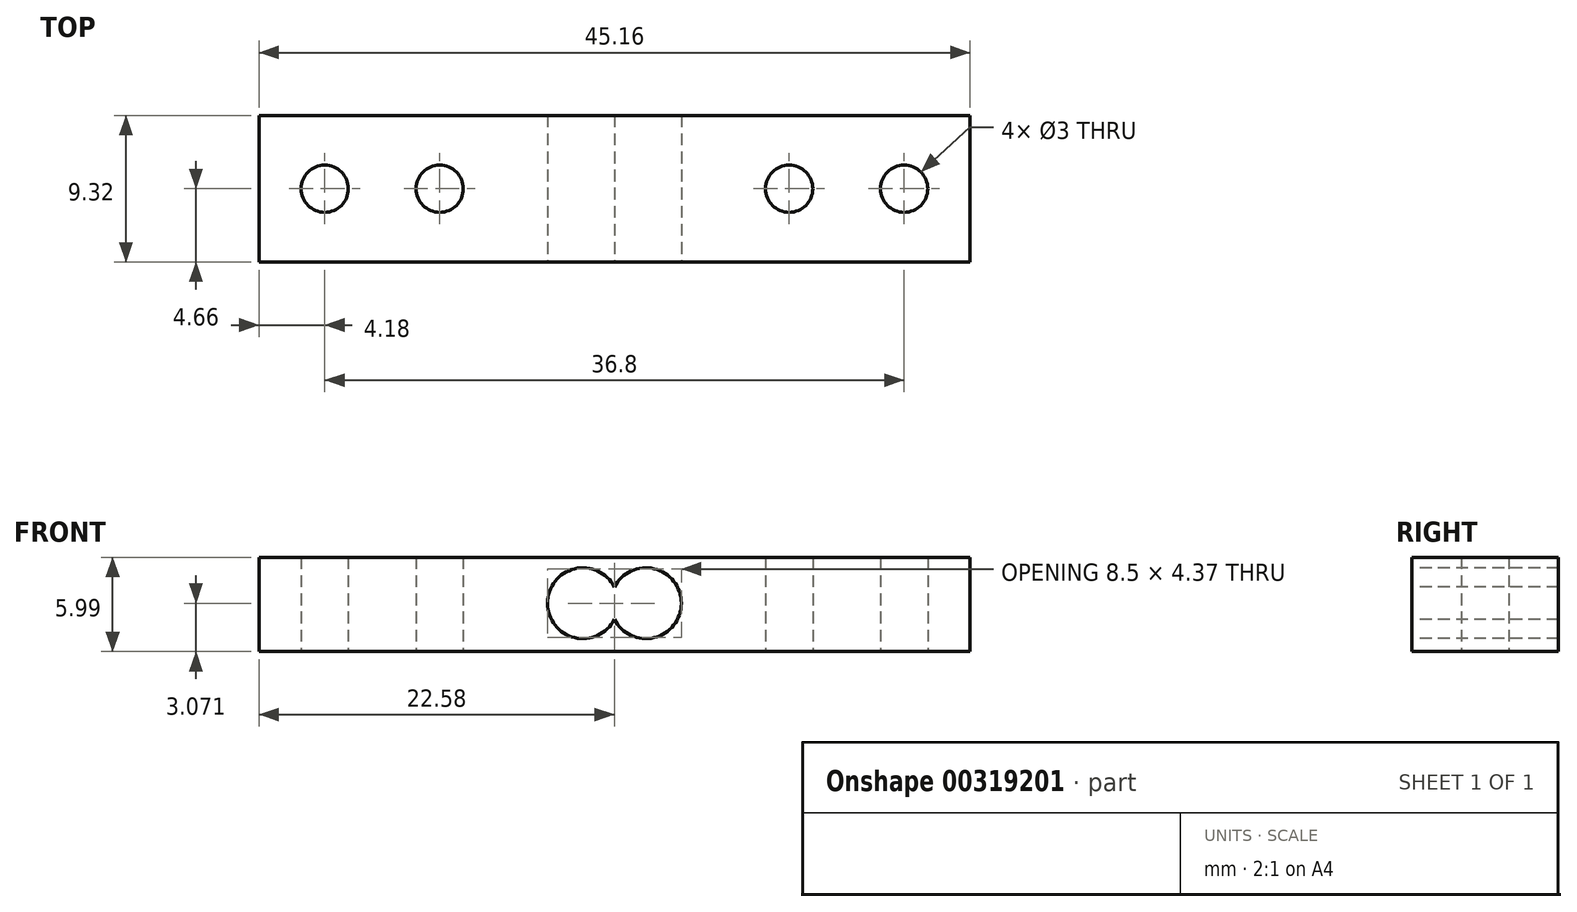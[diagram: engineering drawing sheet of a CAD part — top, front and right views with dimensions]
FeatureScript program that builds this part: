
annotation { "Feature Type Name" : "Feature", "Feature Type Description" : "" }
export const myFeature = defineFeature(function(context is Context, id is Id, definition is map)
    precondition{}
    {
        {
            var Q0;
            Q0=qCreatedBy(makeId("Top.planeOp"),FACE);
            var sketch = newSketch(context, id + "F0", { "sketchPlane" : qUnion([Q0])});
            skLineSegment(sketch, "E0.bottom", {"start": v(-22.58, 4.66) * mm, "end": v(22.58, 4.66) * mm});
            skLineSegment(sketch, "E0.top", {"start": v(-22.58, -4.66) * mm, "end": v(22.58, -4.66) * mm});
            skLineSegment(sketch, "E0.left", {"start": v(-22.58, 4.66) * mm, "end": v(-22.58, -4.66) * mm});
            skLineSegment(sketch, "E0.right", {"start": v(22.58, 4.66) * mm, "end": v(22.58, -4.66) * mm});
            skLineSegment(sketch, "E1", {"start": v(0, 4.66) * mm, "end": v(0, -4.66) * mm, "construction": true});
            skCircle(sketch, "E2", {"center": v(-18.4, 0) * mm, "radius": 1.5 * mm});
            skPoint(sketch, "E2.centerSnap0", {"position": v(-22.58, 0) * mm});
            skCircle(sketch, "E3", {"center": v(-11.1, 0) * mm, "radius": 1.5 * mm});
            skCircle(sketch, "E4.MirrorC", {"center": v(11.1, 0) * mm, "radius": 1.5 * mm});
            skCircle(sketch, "E5.MirrorC", {"center": v(18.4, 0) * mm, "radius": 1.5 * mm});
            skSolve(sketch);
        }
        {
            var Q0;
            Q0 = qSketchRegion(id + "F0", true);
            extrude(context, id + "F1", {"entities" : qUnion([Q0]), "depth" : 6 * mm});
        }
        {
            var Q0;
            Q0=makeQuery(id+"F1.opExtrude","SWEPT_FACE",FACE,{"disambiguationData":[OSD([sQuery(id+"F0.wireOp",EDGE,"E0.top")])]});
            var sketch = newSketch(context, id + "F2", { "sketchPlane" : qUnion([Q0])});
            skCircle(sketch, "E6", {"center": v(-2, 3.07) * mm, "radius": 2.25 * mm});
            skCircle(sketch, "E7", {"center": v(2, 3.07) * mm, "radius": 2.25 * mm});
            skSolve(sketch);
        }
        {
            var Q0;
            Q0 = qSketchRegion(id + "F2", true);
            extrude(context, id + "F3", {"entities" : qUnion([Q0]), "operationType" : NewBodyOperationType.REMOVE, "oppositeDirection" : true, "depth" : 25 * mm});
        }
    });
